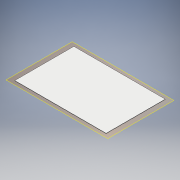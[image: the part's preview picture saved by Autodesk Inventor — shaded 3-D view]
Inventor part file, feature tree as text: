
AUTODESK INVENTOR PART (.ipt)
format: ipt  version: 2017 (Build 210142000, 142)  size: 95,744 bytes
history: native  units: mm
features: other x3, plane x1, extrude x1, sketch x1
ambient origin geometry x8: Origin, YZ Plane, XZ Plane, XY Plane, X Axis, Y Axis, Z Axis, Center Point
bodies: Solid1 (feature_tree)
feature tree (6):
  plane  "Work Plane1"
  extrude  "Extrusion1"  Depth=55.0mm
  sketch  "Sketch1"  dims[d3=85.0mm d4=55.0mm d5=0.3mm d6=0.0mm]
  parser-record x1  (decoder bookkeeping rows leaked as tree rows — omitted from the tree; the rows remain in map.json)
  other  "protoswitchboard.iam"
  other  "cover:1"
note: 1 file-system path scrubbed to <path> (originals preserved in map.json)
